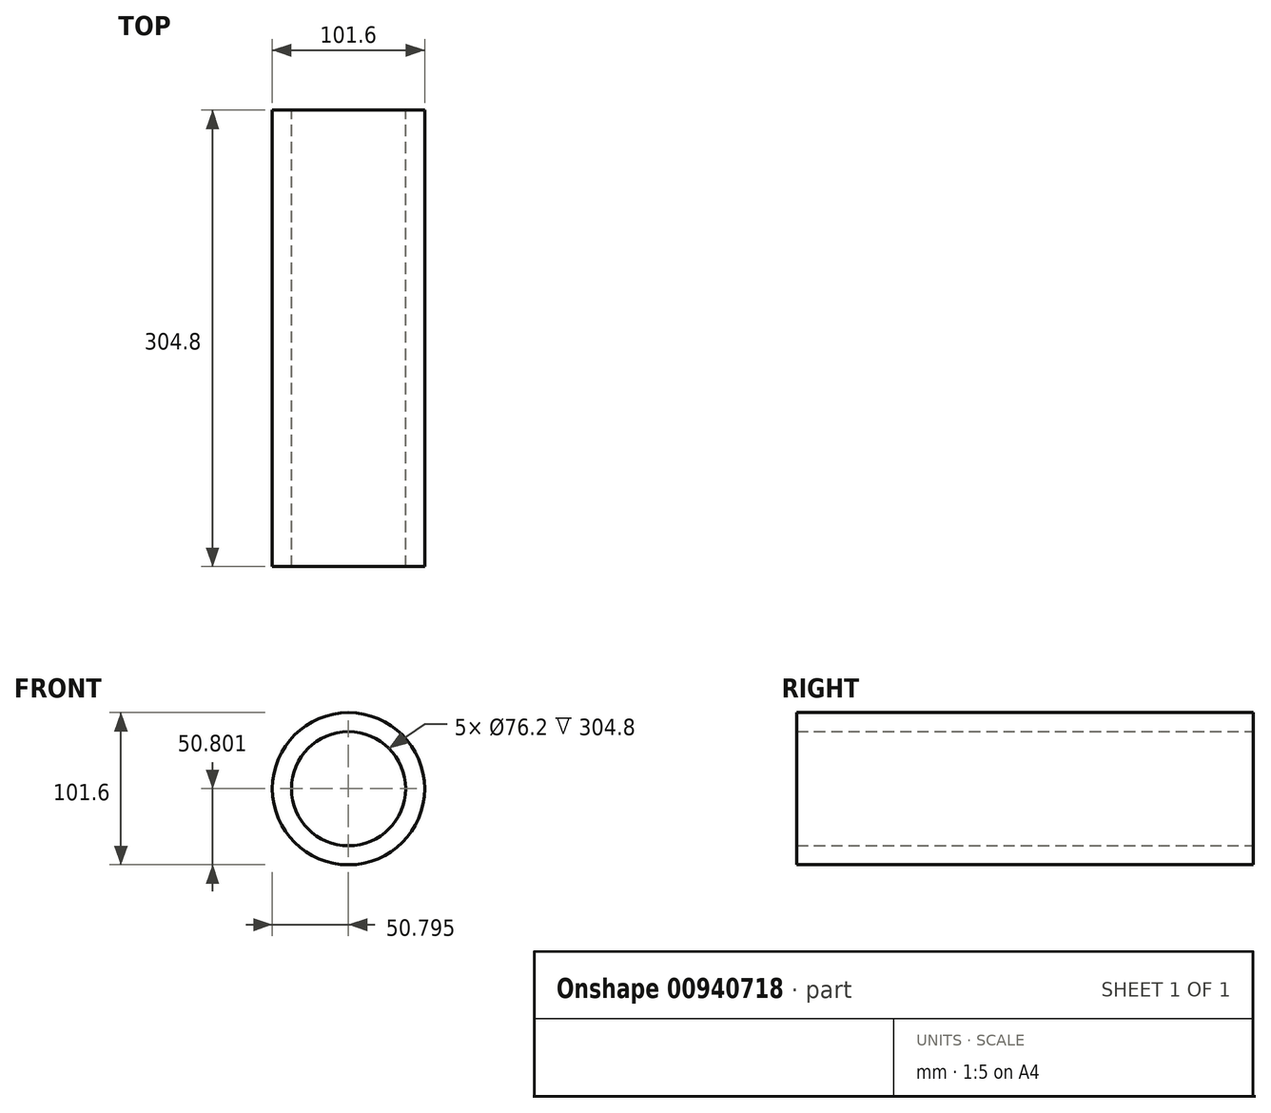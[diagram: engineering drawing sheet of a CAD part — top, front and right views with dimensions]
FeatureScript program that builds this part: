
annotation { "Feature Type Name" : "Feature", "Feature Type Description" : "" }
export const myFeature = defineFeature(function(context is Context, id is Id, definition is map)
    precondition{}
    {
        {
            var Q0;
            Q0=qCreatedBy(makeId("Front.planeOp"),FACE);
            var sketch = newSketch(context, id + "F0", { "sketchPlane" : qUnion([Q0])});
            skCircle(sketch, "E0", {"center": v(-86.32, 35.61) * mm, "radius": 38.1 * mm});
            skCircle(sketch, "E1", {"center": v(-86.32, 35.61) * mm, "radius": 50.8 * mm});
            skSolve(sketch);
        }
        {
            var Q0;
            Q0=makeQuery(id+"F0.imprint","IMPRINT",FACE,{"disambiguationData":[TD([[makeQuery(id+"F0.imprint","IMPRINT",EDGE,{"derivedFrom":sQuery(id+"F0.wireOp",EDGE,"E0")}),-1.0]])]});
            extrude(context, id + "F1", {"entities" : qUnion([Q0]), "depth" : 304.8 * mm, "offsetDistance" : 25.4 * mm});
        }
    });
